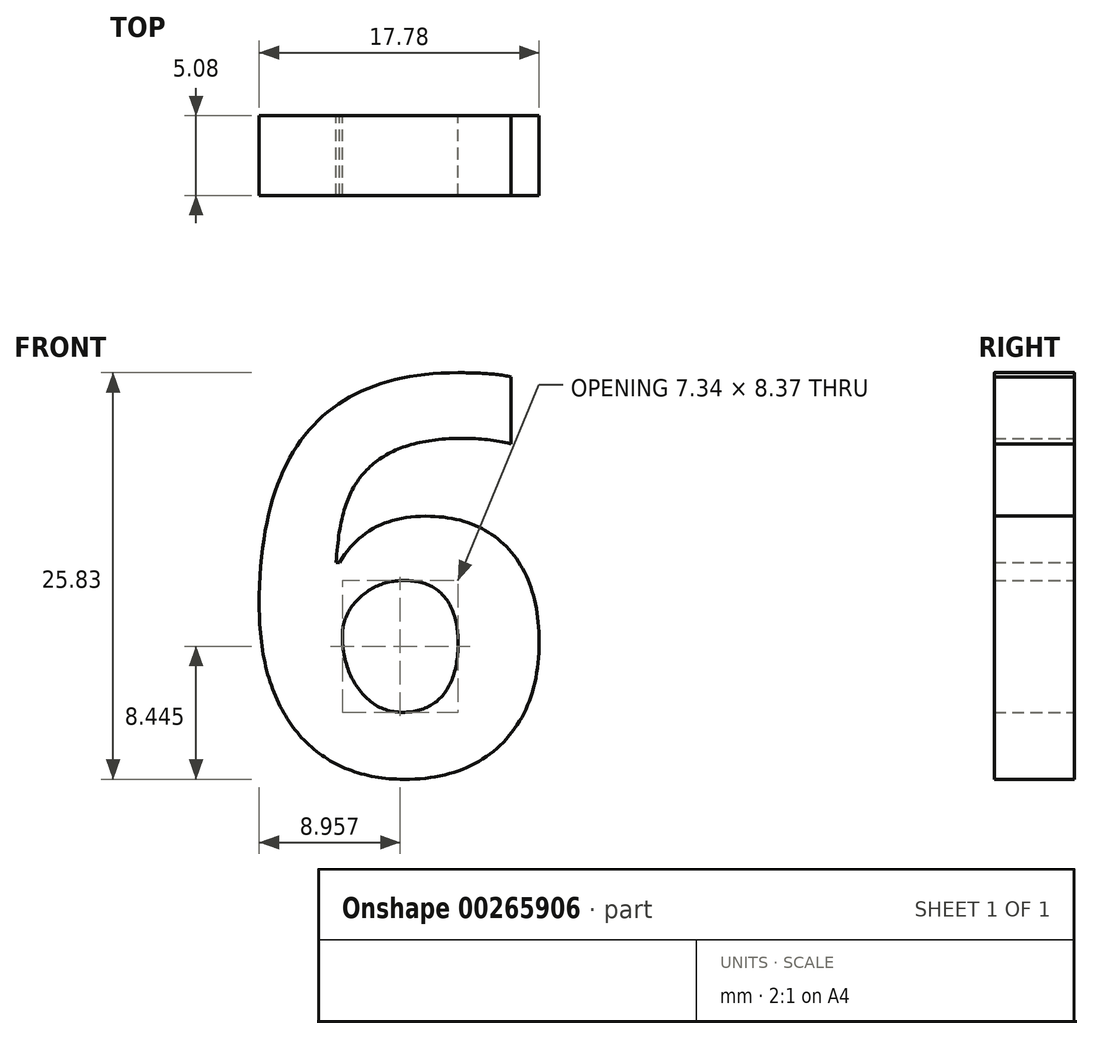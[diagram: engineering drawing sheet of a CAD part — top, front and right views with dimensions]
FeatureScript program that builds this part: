
annotation { "Feature Type Name" : "Feature", "Feature Type Description" : "" }
export const myFeature = defineFeature(function(context is Context, id is Id, definition is map)
    precondition{}
    {
        {
            var Q0;
            Q0=qCreatedBy(makeId("Front.planeOp"),FACE);
            var sketch = newSketch(context, id + "F0", { "sketchPlane" : qUnion([Q0])});
            skText(sketch, "E0", { "text": "6", "fontName": "OpenSans-Bold.ttf"});
            const initialGuessF0  = {"E0": [-0.06562, 0.02697, 1, 0, 0.0254]};
            skSetInitialGuess(sketch, initialGuessF0);
            skSolve(sketch);
        }
        {
            var Q0;
            Q0 = qSketchRegion(id + "F0", true);
            extrude(context, id + "F1", {"entities" : qUnion([Q0]), "depth" : 5.08 * mm});
        }
    });
